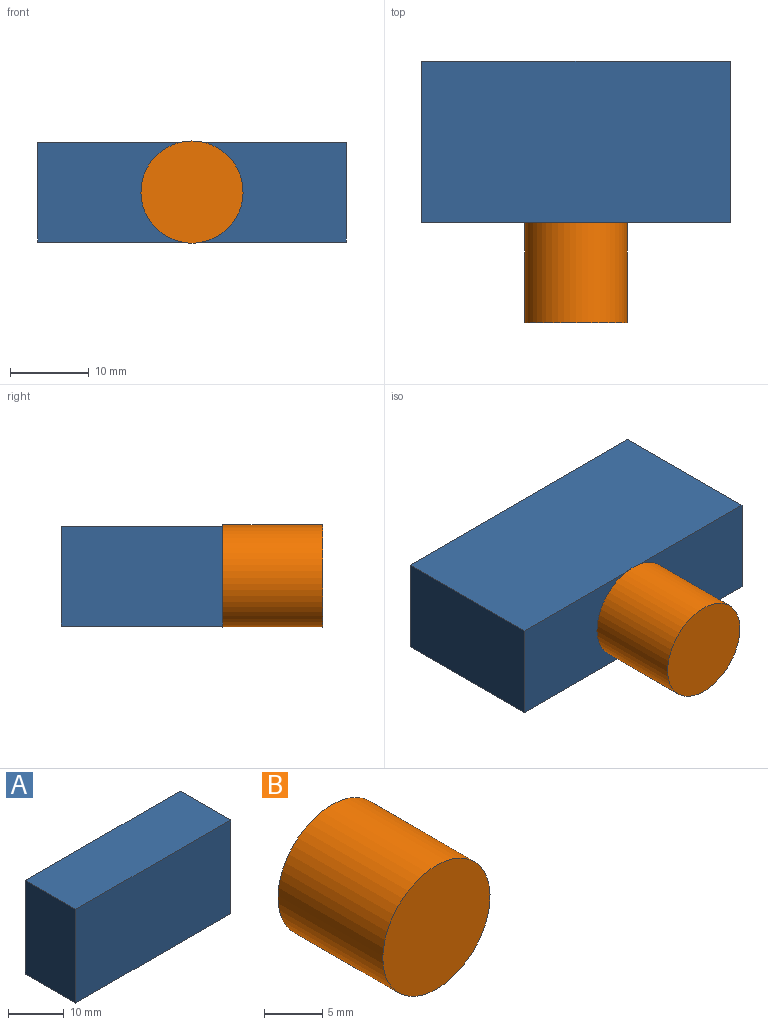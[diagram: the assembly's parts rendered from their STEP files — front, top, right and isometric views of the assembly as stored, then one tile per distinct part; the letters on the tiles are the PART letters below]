
ASSEMBLY  parts=2 mates=1
PART A: 6 faces, bbox 39.2x12.7x20.5 mm
  f0: plane 20.51x12.7mm, normal (-1,0,0), area 260.4mm2, adj f1,f3,f4,f5
  f1: plane 39.15x12.7mm, normal (0,0,-1), area 497.2mm2, adj f0,f2,f4,f5
  f2: plane 20.51x12.7mm, normal (1,0,0), area 260.4mm2, adj f1,f3,f4,f5
  f3: plane 39.15x12.7mm, normal (0,0,1), area 497.2mm2, adj f0,f2,f4,f5
  f4: plane 39.15x20.51mm, normal (0,-1,0), area 802.9mm2, adj f0,f1,f2,f3
  f5: plane 39.15x20.51mm, normal (0,1,0), area 802.9mm2, adj f0,f1,f2,f3
PART B: 3 faces, bbox 13x12.7x13 mm
  f0: cylinder r=6.49mm len=12.98mm, axis (0,1,0), area 517.8mm2, adj f1,f2
  f1: plane 12.98x12.98mm, normal (0,-1,0), area 132.3mm2, adj f0
  f2: plane 12.98x12.98mm, normal (0,1,0), area 132.3mm2, adj f0
PLACE A rot(axis=(1,0,0),90deg) t=(34.11,60.01,68.68)mm
PLACE B rot(axis=(1,0,0),180deg) t=(0,-25.4,124.66)mm
MATE fastened A.f3 <-> B.f0  axis (0,1,0) through (-15.91,-12.7,62.33)mm
